# Revit family: P200921MX-005c_MDB8959SK_BWZ
name_source: partatom
category: Specialty Equipment
units: mm (PartAtom-declared; Revit-internal decimal feet)

## family parameters
Always vertical = Yes
Cut with Voids When Loaded = No
Enable Cutting in Views = No
Maintain Annotation Orientation = No
Part Type = Normal
Room Calculation Point = No
Round Connector Dimension = Use Diameter
Shared = No
Work Plane-Based = No

## types (3) — shared parameters
Accent Material = ARCAT - Metal - Steel - Black
Amps = 0 A
Base Fitting Material = ARCAT - Metal - Plastic - Cream
Blanket Material = ARCAT - Fabric - Grey
Body Material = ARCAT - Metal - Plastic - Grey
Clearance Material = ARCAT - Clearance
Default Elevation = 0"
Depth = 24 1/2"
Description = Top control dishwasher with Third Level Rack and Dual Power filtration
Lave-vaisselle à panier de troisième niveau et filtration à puissance double
Dimension Guide = https://www.whirlpool.com
https://www.whirlpool.com
Energy Guide = https://www.whirlpool.com
https://www.whirlpool.com
Family Name = Cleaning
Feature 1 = Dual Power Filtration
Filtration à puissance double
Feature 2 = Steam Sanitize option
Option d'assainissement à la vapeur
Feature 3 = 3rd Level Rack
Panier de 3ᵉ niveau
Height = 34 1/2"
Manufacturer = Maytag
Voltage = 0 V
Width = 23 7/8"

## per-type parameters (varying)
| type | Black Logo | Bottom Panel Material | Display Panel Material | Door Material | Handle Material | White Logo |
| MDB8959SKZ | No | ARCAT - Metal - Steel - Black | ARCAT - Glass - Black | ARCAT - Metal - Steel - Stainless | ARCAT - Metal - Steel - Stainless | Yes |
| MDB8959SKB | No | ARCAT - Metal - Steel - Black | ARCAT - Glass - Black | ARCAT - Metal - Steel - Stainless - Black | ARCAT - Metal - Steel - Stainless - Black | Yes |
| MDB8959SKW | Yes | ARCAT - Metal - Steel - White | ARCAT - Glass - White | ARCAT - Metal - Steel - Stainless - White | ARCAT - Metal - Steel - Stainless - White | No |

note: column(s) folded — value = type name in every type: Model

## geometry (parser evidence)
native form markers: Sweep x5
no freeform markers — native parametric forms only
